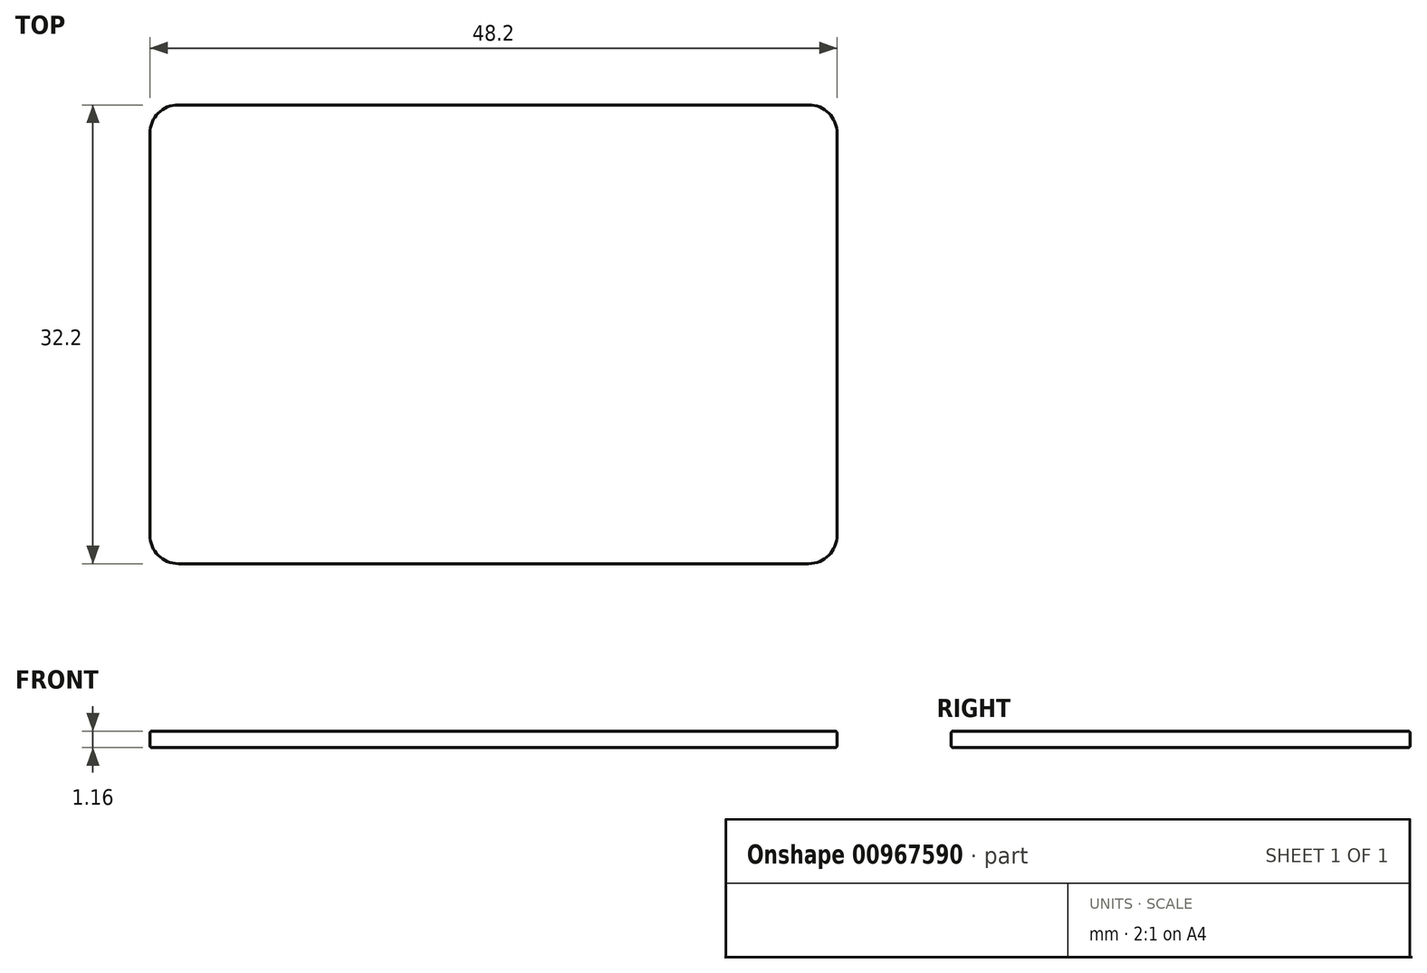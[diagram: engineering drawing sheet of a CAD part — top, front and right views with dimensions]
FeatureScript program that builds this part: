
annotation { "Feature Type Name" : "Feature", "Feature Type Description" : "" }
export const myFeature = defineFeature(function(context is Context, id is Id, definition is map)
    precondition{}
    {
        {
            var Q0;
            Q0=qCreatedBy(makeId("Top.planeOp"),FACE);
            var sketch = newSketch(context, id + "F0", { "sketchPlane" : qUnion([Q0])});
            skLineSegment(sketch, "E0.bottom", {"start": v(22.1, -16.1) * mm, "end": v(-22.1, -16.1) * mm});
            skLineSegment(sketch, "E0.top", {"start": v(22.1, 16.1) * mm, "end": v(-22.1, 16.1) * mm});
            skLineSegment(sketch, "E0.left", {"start": v(24.1, -14.1) * mm, "end": v(24.1, 14.1) * mm});
            skLineSegment(sketch, "E0.right", {"start": v(-24.1, -14.1) * mm, "end": v(-24.1, 14.1) * mm});
            skPoint(sketch, "E0.middle", {"position": v(0, 0) * mm});
            skPoint(sketch, "E1.visualSharp", {"position": v(-24.1, 16.1) * mm});
            skArc(sketch, "E1.filletArc", {"start": v(-22.1, 16.1) * mm, "mid": v(-23.51, 15.51) * mm, "end": v(-24.1, 14.1) * mm});
            skPoint(sketch, "E2.visualSharp", {"position": v(24.1, 16.1) * mm});
            skArc(sketch, "E2.filletArc", {"start": v(24.1, 14.1) * mm, "mid": v(23.51, 15.51) * mm, "end": v(22.1, 16.1) * mm});
            skPoint(sketch, "E3.visualSharp", {"position": v(24.1, -16.1) * mm});
            skArc(sketch, "E3.filletArc", {"start": v(22.1, -16.1) * mm, "mid": v(23.51, -15.51) * mm, "end": v(24.1, -14.1) * mm});
            skPoint(sketch, "E4.visualSharp", {"position": v(-24.1, -16.1) * mm});
            skArc(sketch, "E4.filletArc", {"start": v(-24.1, -14.1) * mm, "mid": v(-23.51, -15.51) * mm, "end": v(-22.1, -16.1) * mm});
            skSolve(sketch);
        }
        {
            var Q0;
            Q0 = qSketchRegion(id + "F0", true);
            extrude(context, id + "F1", {"entities" : qUnion([Q0]), "depth" : 1.15 * mm, "offsetDistance" : 25 * mm, "symmetric" : true});
        }
        {
            var Q0;
            Q0=makeQuery(id+"F1.opExtrude","CAP_FACE",FACE,{"disambiguationData":[OSD([sQuery(id+"F0.wireOp",EDGE,"E0.bottom"),sQuery(id+"F0.wireOp",EDGE,"E0.top"),sQuery(id+"F0.wireOp",EDGE,"E0.left"),sQuery(id+"F0.wireOp",EDGE,"E0.right"),sQuery(id+"F0.wireOp",EDGE,"E1.filletArc"),sQuery(id+"F0.wireOp",EDGE,"E2.filletArc"),sQuery(id+"F0.wireOp",EDGE,"E3.filletArc"),sQuery(id+"F0.wireOp",EDGE,"E4.filletArc")])],"isStart":true});
            var Q1;
            Q1=makeQuery(id+"F1.opExtrude","CAP_FACE",FACE,{"disambiguationData":[OSD([sQuery(id+"F0.wireOp",EDGE,"E0.bottom"),sQuery(id+"F0.wireOp",EDGE,"E0.top"),sQuery(id+"F0.wireOp",EDGE,"E0.left"),sQuery(id+"F0.wireOp",EDGE,"E0.right"),sQuery(id+"F0.wireOp",EDGE,"E1.filletArc"),sQuery(id+"F0.wireOp",EDGE,"E2.filletArc"),sQuery(id+"F0.wireOp",EDGE,"E3.filletArc"),sQuery(id+"F0.wireOp",EDGE,"E4.filletArc")])],"isStart":false});
            fillet(context, id + "F2", {"entities" : qUnion([Q0, Q1]), "radius" : 0.15 * mm, "tangentPropagation" : true, "allowEdgeOverflow" : false});
        }
    });
